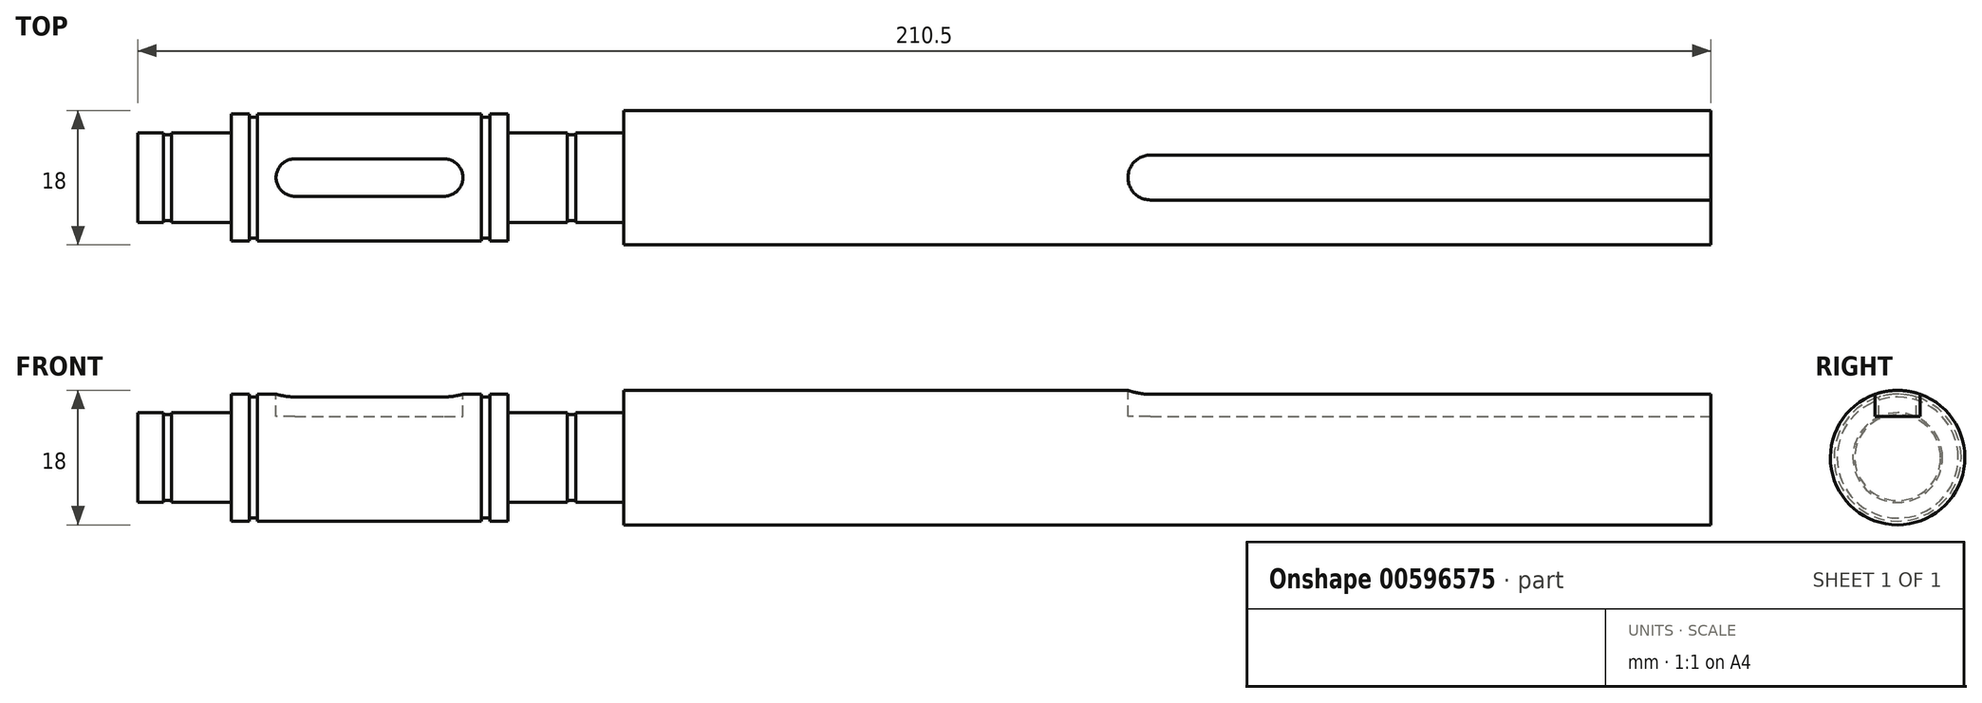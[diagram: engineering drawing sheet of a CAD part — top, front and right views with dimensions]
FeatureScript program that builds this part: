
annotation { "Feature Type Name" : "Feature", "Feature Type Description" : "" }
export const myFeature = defineFeature(function(context is Context, id is Id, definition is map)
    precondition{}
    {
        {
            var Q0;
            Q0=qCreatedBy(makeId("Front.planeOp"),FACE);
            var sketch = newSketch(context, id + "F0", { "sketchPlane" : qUnion([Q0])});
            skLineSegment(sketch, "E0", {"start": v(2.25, 0) * mm, "end": v(64.25, 0) * mm});
            skLineSegment(sketch, "E1", {"start": v(62.25, 6) * mm, "end": v(60.85, 6) * mm});
            skLineSegment(sketch, "E2", {"start": v(51.75, 6) * mm, "end": v(51.75, 8.5) * mm});
            skLineSegment(sketch, "E3", {"start": v(51.75, 8.5) * mm, "end": v(49.35, 8.5) * mm});
            skLineSegment(sketch, "E4", {"start": v(49.35, 8.5) * mm, "end": v(49.35, 8.1) * mm});
            skLineSegment(sketch, "E5", {"start": v(49.35, 8.1) * mm, "end": v(48.25, 8.1) * mm});
            skLineSegment(sketch, "E6", {"start": v(48.25, 8.1) * mm, "end": v(48.25, 8.5) * mm});
            skLineSegment(sketch, "E7", {"start": v(48.25, 8.5) * mm, "end": v(18.25, 8.5) * mm});
            skLineSegment(sketch, "E8", {"start": v(18.25, 8.5) * mm, "end": v(18.25, 8.1) * mm});
            skLineSegment(sketch, "E9", {"start": v(18.25, 8.1) * mm, "end": v(17.15, 8.1) * mm});
            skLineSegment(sketch, "E10", {"start": v(17.15, 8.1) * mm, "end": v(17.15, 8.5) * mm});
            skLineSegment(sketch, "E11", {"start": v(17.15, 8.5) * mm, "end": v(14.75, 8.5) * mm});
            skLineSegment(sketch, "E12", {"start": v(14.75, 8.5) * mm, "end": v(14.75, 6) * mm});
            skLineSegment(sketch, "E13", {"start": v(14.75, 6) * mm, "end": v(6.75, 6) * mm});
            skLineSegment(sketch, "E14", {"start": v(6.75, 6) * mm, "end": v(6.75, 5.75) * mm});
            skLineSegment(sketch, "E15", {"start": v(6.75, 5.75) * mm, "end": v(5.65, 5.75) * mm});
            skLineSegment(sketch, "E16", {"start": v(5.65, 5.75) * mm, "end": v(5.65, 6) * mm});
            skLineSegment(sketch, "E17", {"start": v(5.65, 6) * mm, "end": v(2.25, 6) * mm});
            skLineSegment(sketch, "E18", {"start": v(2.25, 6) * mm, "end": v(2.25, 0) * mm});
            skLineSegment(sketch, "E19", {"start": v(59.75, 5.75) * mm, "end": v(60.85, 5.75) * mm});
            skLineSegment(sketch, "E20", {"start": v(59.75, 5.75) * mm, "end": v(59.75, 6) * mm});
            skLineSegment(sketch, "E21", {"start": v(60.85, 5.75) * mm, "end": v(60.85, 6) * mm});
            skLineSegment(sketch, "E22.trimOffspring", {"start": v(59.75, 6) * mm, "end": v(51.75, 6) * mm});
            skLineSegment(sketch, "E23", {"start": v(64.25, 0) * mm, "end": v(81.75, 0) * mm});
            skLineSegment(sketch, "E24", {"start": v(81.75, 0) * mm, "end": v(192.75, 0) * mm});
            skLineSegment(sketch, "E25", {"start": v(67.25, 9) * mm, "end": v(192.75, 9) * mm});
            skPoint(sketch, "E26.end.orphan", {"position": v(81.75, 6) * mm});
            skLineSegment(sketch, "E27.0", {"start": v(67.25, 6) * mm, "end": v(67.25, 9) * mm});
            skLineSegment(sketch, "E28", {"start": v(62.25, 6) * mm, "end": v(67.25, 6) * mm});
            skLineSegment(sketch, "E29.0", {"start": v(212.75, 9) * mm, "end": v(212.75, 6) * mm});
            skLineSegment(sketch, "E30.0", {"start": v(212.75, 6) * mm, "end": v(212.75, 0) * mm});
            skLineSegment(sketch, "E31", {"start": v(192.75, 9) * mm, "end": v(212.75, 9) * mm});
            skLineSegment(sketch, "E32", {"start": v(192.75, 0) * mm, "end": v(212.75, 0) * mm});
            skSolve(sketch);
        }
        {
            var Q0;
            Q0=makeQuery(id+"F0.imprint","IMPRINT",FACE,{"disambiguationData":[TD([[makeQuery(id+"F0.imprint","IMPRINT",EDGE,{"derivedFrom":sQuery(id+"F0.wireOp",EDGE,"E0")}),1.0]])]});
            var Q1;
            Q1=sQuery(id+"F0.wireOp",EDGE,"E0");
            revolve(context, id + "F1", {"entities" : qUnion([Q0]), "axis" : qUnion([Q1]), "revolveType" : RevolveType.FULL});
        }
        {
            var Q0;
            Q0=qCreatedBy(makeId("Top.planeOp"),FACE);
            cPlane(context, id + "F2", {"entities" : qUnion([Q0]), "cplaneType" : CPlaneType.OFFSET, "offset" : (17 / 2) * mm, "width" : 150 * mm, "height" : 150 * mm});
        }
        {
            var Q0;
            Q0=qCreatedBy(id+"F2.planeOp",FACE);
            var sketch = newSketch(context, id + "F3", { "sketchPlane" : qUnion([Q0])});
            skArc(sketch, "E33", {"start": v(23.25, 2.5) * mm, "mid": v(20.75, 0) * mm, "end": v(23.25, -2.5) * mm});
            skArc(sketch, "E34", {"start": v(43.25, -2.5) * mm, "mid": v(45.75, 0) * mm, "end": v(43.25, 2.5) * mm});
            skLineSegment(sketch, "E35", {"start": v(23.25, 2.5) * mm, "end": v(43.25, 2.5) * mm});
            skLineSegment(sketch, "E36", {"start": v(23.25, -2.5) * mm, "end": v(43.25, -2.5) * mm});
            skSolve(sketch);
        }
        {
            var Q0;
            Q0=makeQuery(id+"F3.imprint","IMPRINT",FACE,{"disambiguationData":[TD([[makeQuery(id+"F3.imprint","IMPRINT",EDGE,{"derivedFrom":sQuery(id+"F3.wireOp",EDGE,"E33")}),1.0]])]});
            extrude(context, id + "F4", {"entities" : qUnion([Q0]), "operationType" : NewBodyOperationType.REMOVE, "oppositeDirection" : true, "depth" : 3 * mm, "offsetDistance" : 25 * mm});
        }
        {
            var Q0;
            Q0=qCreatedBy(makeId("Top.planeOp"),FACE);
            cPlane(context, id + "F5", {"entities" : qUnion([Q0]), "cplaneType" : CPlaneType.OFFSET, "offset" : 9 * mm, "width" : 150 * mm, "height" : 150 * mm});
        }
        {
            var Q0;
            Q0=qCreatedBy(id+"F5.planeOp",FACE);
            var sketch = newSketch(context, id + "F6", { "sketchPlane" : qUnion([Q0])});
            skArc(sketch, "E37", {"start": v(137.75, 3) * mm, "mid": v(134.75, 0) * mm, "end": v(137.75, -3) * mm});
            skLineSegment(sketch, "E38", {"start": v(137.75, 3) * mm, "end": v(212.75, 3) * mm});
            skLineSegment(sketch, "E39", {"start": v(137.75, -3) * mm, "end": v(212.75, -3) * mm});
            skLineSegment(sketch, "E40", {"start": v(212.75, -3) * mm, "end": v(212.75, 3) * mm});
            skPoint(sketch, "E41.orphan", {"position": v(135.54, 3) * mm});
            skSolve(sketch);
        }
        {
            var Q0;
            Q0=makeQuery(id+"F6.imprint","IMPRINT",FACE,{"disambiguationData":[TD([[makeQuery(id+"F6.imprint","IMPRINT",EDGE,{"derivedFrom":sQuery(id+"F6.wireOp",EDGE,"E37")}),1.0]])]});
            extrude(context, id + "F7", {"entities" : qUnion([Q0]), "operationType" : NewBodyOperationType.REMOVE, "oppositeDirection" : true, "depth" : 3.5 * mm, "offsetDistance" : 25 * mm});
        }
    });
